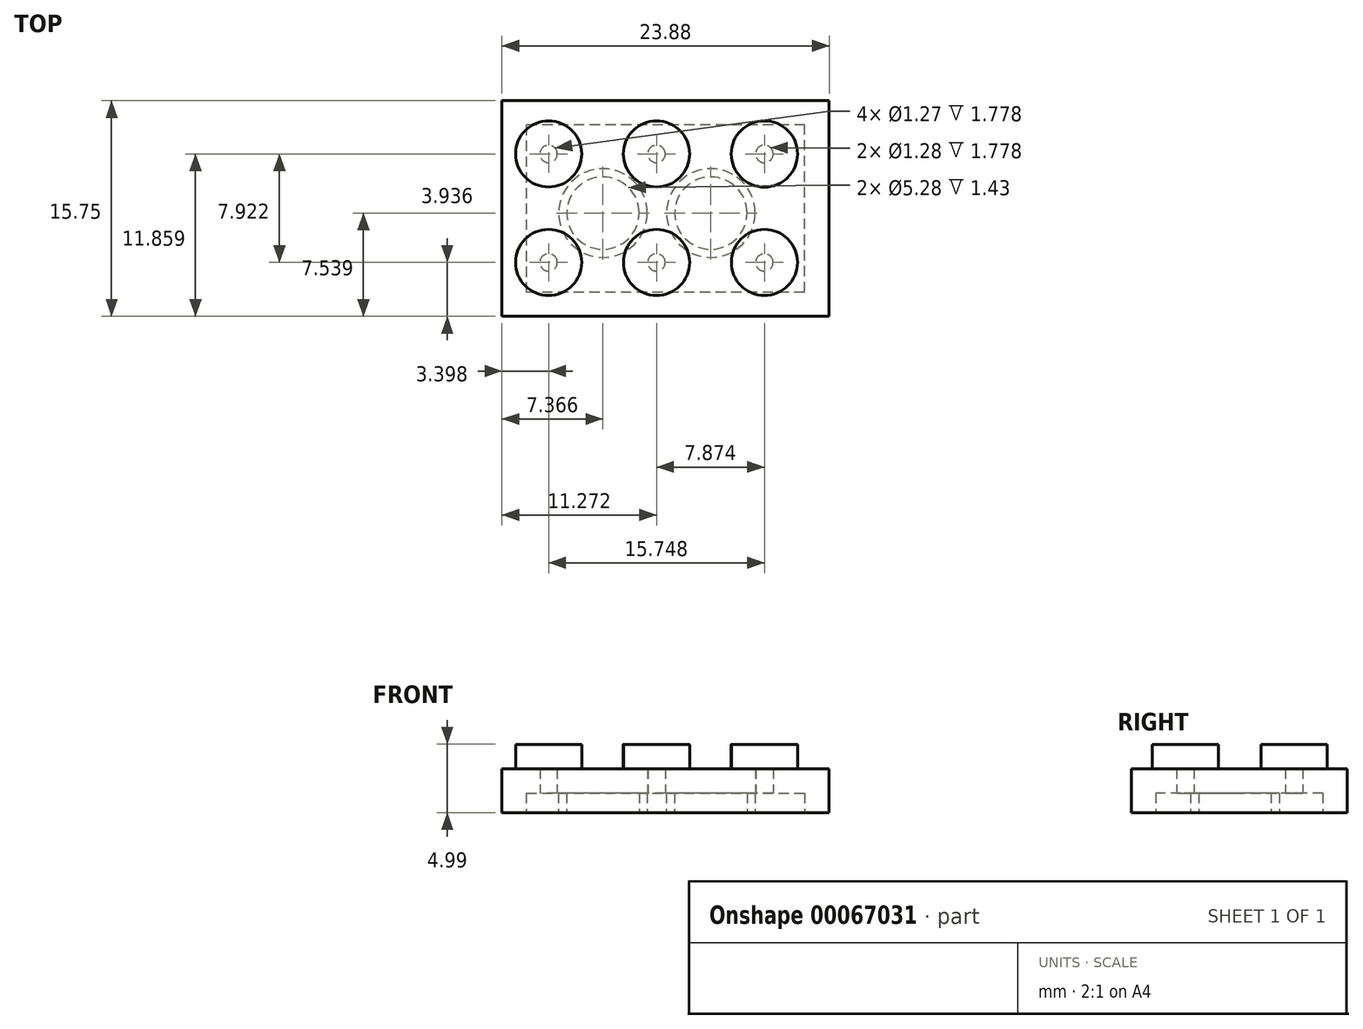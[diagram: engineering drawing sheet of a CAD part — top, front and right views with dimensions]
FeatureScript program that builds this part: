
annotation { "Feature Type Name" : "Feature", "Feature Type Description" : "" }
export const myFeature = defineFeature(function(context is Context, id is Id, definition is map)
    precondition{}
    {
        {
            var Q0;
            Q0=qCreatedBy(makeId("Top.planeOp"),FACE);
            var sketch = newSketch(context, id + "F0", { "sketchPlane" : qUnion([Q0])});
            skLineSegment(sketch, "E0", {"start": v(0, 0) * mm, "end": v(23.88, 0) * mm});
            skLineSegment(sketch, "E1", {"start": v(23.88, 0) * mm, "end": v(23.88, 15.75) * mm});
            skLineSegment(sketch, "E2", {"start": v(23.88, 15.75) * mm, "end": v(0, 15.75) * mm});
            skLineSegment(sketch, "E3", {"start": v(0, 15.75) * mm, "end": v(0, 0) * mm});
            skSolve(sketch);
        }
        {
            var Q0;
            Q0=makeQuery(id+"F0.imprint","IMPRINT",FACE,{"disambiguationData":[TD([[makeQuery(id+"F0.imprint","IMPRINT",EDGE,{"derivedFrom":sQuery(id+"F0.wireOp",EDGE,"E0")}),1.0]])]});
            var Q1;
            Q1 = qSketchRegion(id + "F2", true);
            extrude(context, id + "F1", {"entities" : qUnion([Q0, Q1]), "depth" : 3.2 * mm});
        }
        {
            var Q0;
            Q0=makeQuery(id+"F1.opExtrude","CAP_FACE",FACE,{"disambiguationData":[OSD([sQuery(id+"F0.wireOp",EDGE,"E0"),sQuery(id+"F0.wireOp",EDGE,"E1"),sQuery(id+"F0.wireOp",EDGE,"E2"),sQuery(id+"F0.wireOp",EDGE,"E3")])],"isStart":false});
            var sketch = newSketch(context, id + "F2", { "sketchPlane" : qUnion([Q0])});
            skCircle(sketch, "E4", {"center": v(3.4, 11.86) * mm, "radius": 2.41 * mm});
            skCircle(sketch, "E5", {"center": v(11.27, 11.86) * mm, "radius": 2.42 * mm});
            skCircle(sketch, "E6", {"center": v(19.15, 11.86) * mm, "radius": 2.42 * mm});
            skCircle(sketch, "E7", {"center": v(3.4, 3.94) * mm, "radius": 2.41 * mm});
            skCircle(sketch, "E8", {"center": v(11.27, 3.94) * mm, "radius": 2.41 * mm});
            skCircle(sketch, "E9", {"center": v(19.15, 3.94) * mm, "radius": 2.41 * mm});
            skSolve(sketch);
        }
        {
            var Q0;
            Q0=makeQuery(id+"F2.imprint","IMPRINT",FACE,{"disambiguationData":[TD([[makeQuery(id+"F2.imprint","IMPRINT",EDGE,{"derivedFrom":sQuery(id+"F2.wireOp",EDGE,"E4")}),1.0]])]});
            extrude(context, id + "F3", {"entities" : qUnion([Q0]), "operationType" : NewBodyOperationType.ADD, "depth" : 1.78 * mm});
        }
        {
            var Q0;
            Q0=makeQuery(id+"F2.imprint","IMPRINT",FACE,{"disambiguationData":[TD([[makeQuery(id+"F2.imprint","IMPRINT",EDGE,{"derivedFrom":sQuery(id+"F2.wireOp",EDGE,"E5")}),1.0]])]});
            extrude(context, id + "F4", {"entities" : qUnion([Q0]), "operationType" : NewBodyOperationType.ADD, "depth" : 1.78 * mm});
        }
        {
            var Q0;
            Q0=makeQuery(id+"F2.imprint","IMPRINT",FACE,{"disambiguationData":[TD([[makeQuery(id+"F2.imprint","IMPRINT",EDGE,{"derivedFrom":sQuery(id+"F2.wireOp",EDGE,"E6")}),1.0]])]});
            extrude(context, id + "F5", {"entities" : qUnion([Q0]), "operationType" : NewBodyOperationType.ADD, "depth" : 1.78 * mm});
        }
        {
            var Q0;
            Q0=makeQuery(id+"F2.imprint","IMPRINT",FACE,{"disambiguationData":[TD([[makeQuery(id+"F2.imprint","IMPRINT",EDGE,{"derivedFrom":sQuery(id+"F2.wireOp",EDGE,"E7")}),1.0]])]});
            extrude(context, id + "F6", {"entities" : qUnion([Q0]), "operationType" : NewBodyOperationType.ADD, "depth" : 1.78 * mm});
        }
        {
            var Q0;
            Q0=makeQuery(id+"F2.imprint","IMPRINT",FACE,{"disambiguationData":[TD([[makeQuery(id+"F2.imprint","IMPRINT",EDGE,{"derivedFrom":sQuery(id+"F2.wireOp",EDGE,"E8")}),1.0]])]});
            extrude(context, id + "F7", {"entities" : qUnion([Q0]), "operationType" : NewBodyOperationType.ADD, "depth" : 1.78 * mm});
        }
        {
            var Q0;
            Q0=makeQuery(id+"F2.imprint","IMPRINT",FACE,{"disambiguationData":[TD([[makeQuery(id+"F2.imprint","IMPRINT",EDGE,{"derivedFrom":sQuery(id+"F2.wireOp",EDGE,"E9")}),1.0]])]});
            extrude(context, id + "F8", {"entities" : qUnion([Q0]), "operationType" : NewBodyOperationType.ADD, "depth" : 1.78 * mm});
        }
        {
            var Q0;
            Q0=makeQuery(id+"F1.opExtrude","CAP_FACE",FACE,{"disambiguationData":[OSD([sQuery(id+"F0.wireOp",EDGE,"E0"),sQuery(id+"F0.wireOp",EDGE,"E1"),sQuery(id+"F0.wireOp",EDGE,"E2"),sQuery(id+"F0.wireOp",EDGE,"E3")])],"isStart":true});
            shell(context, id + "F9", {"entities" : qUnion([Q0]), "thickness" : 1.78 * mm});
        }
        {
            var Q0;
            Q0=makeQuery(id+"F0.imprint","IMPRINT",FACE,{"disambiguationData":[TD([[makeQuery(id+"F0.imprint","IMPRINT",EDGE,{"derivedFrom":sQuery(id+"F0.wireOp",EDGE,"E0")}),1.0]])]});
            var sketch = newSketch(context, id + "F10", { "sketchPlane" : qUnion([Q0])});
            skCircle(sketch, "E10", {"center": v(7.37, 7.54) * mm, "radius": 3.24 * mm});
            skCircle(sketch, "E11", {"center": v(15.24, 7.54) * mm, "radius": 3.24 * mm});
            skCircle(sketch, "E12", {"center": v(7.37, 7.54) * mm, "radius": 2.64 * mm});
            skCircle(sketch, "E13", {"center": v(15.24, 7.54) * mm, "radius": 2.64 * mm});
            skLineSegment(sketch, "E14", {"start": v(7.37, 7.54) * mm, "end": v(0, 7.54) * mm});
            skSolve(sketch);
        }
        {
            var Q0;
            Q0 = qSketchRegion(id + "F10", true);
            extrude(context, id + "F11", {"entities" : qUnion([Q0]), "operationType" : NewBodyOperationType.ADD, "depth" : 3.07 * mm});
        }
    });
